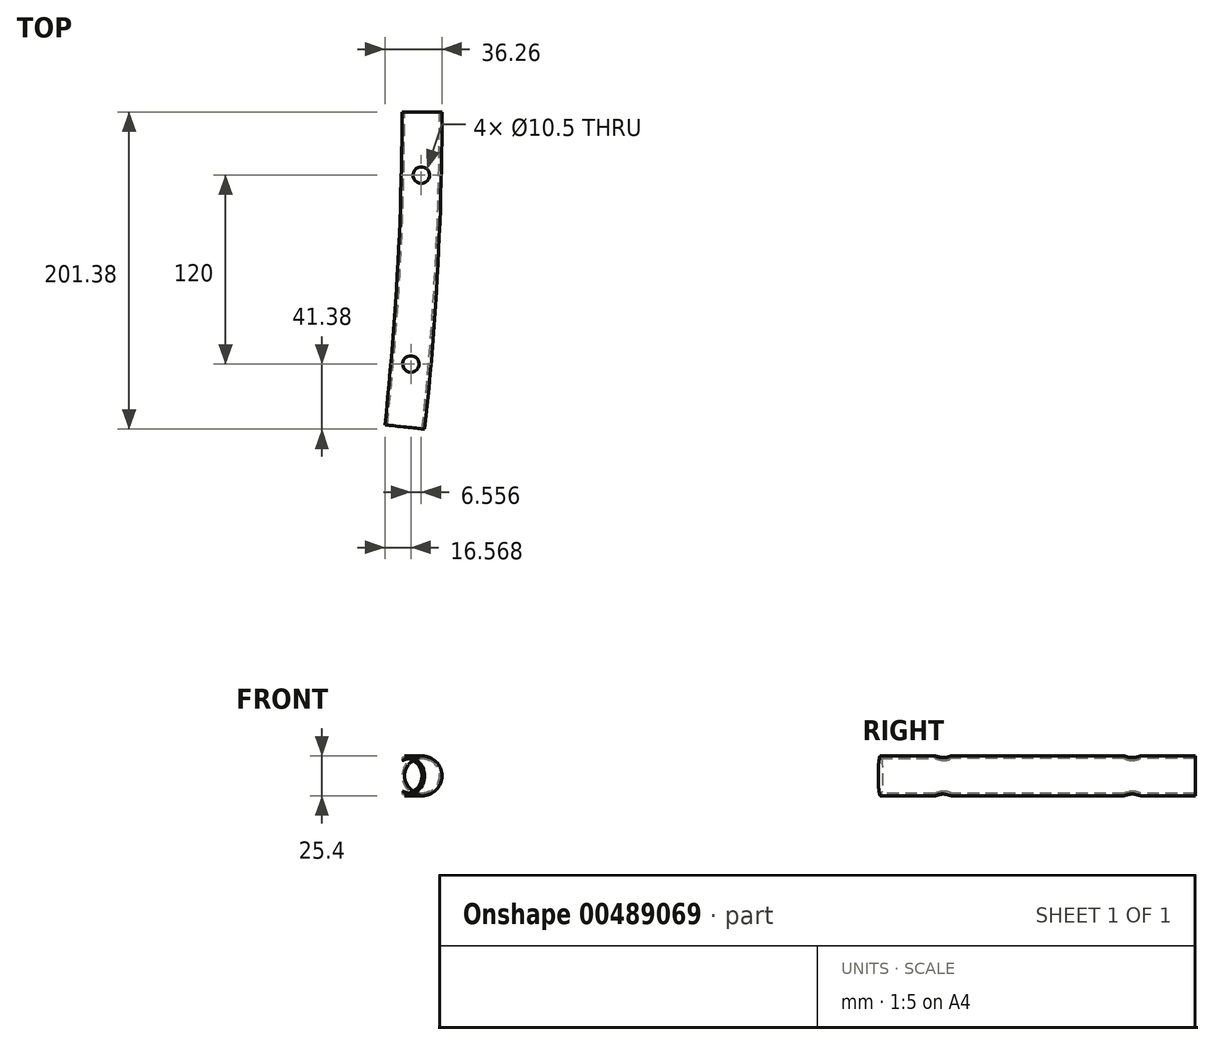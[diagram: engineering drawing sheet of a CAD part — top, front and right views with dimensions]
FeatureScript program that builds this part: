
annotation { "Feature Type Name" : "Feature", "Feature Type Description" : "" }
export const myFeature = defineFeature(function(context is Context, id is Id, definition is map)
    precondition{}
    {
        {
            var Q0;
            Q0=qCreatedBy(makeId("Top.planeOp"),FACE);
            var sketch = newSketch(context, id + "F0", { "sketchPlane" : qUnion([Q0])});
            skArc(sketch, "E0", {"start": v(1823.16, -200) * mm, "mid": v(1831.36, -100.15) * mm, "end": v(1834.1, 0) * mm});
            skSolve(sketch);
        }
        {
            var Q0;
            Q0=qCreatedBy(makeId("Front.planeOp"),FACE);
            var sketch = newSketch(context, id + "F1", { "sketchPlane" : qUnion([Q0])});
            skCircle(sketch, "E1", {"center": v(1834.1, 0) * mm, "radius": 12.7 * mm});
            skCircle(sketch, "E2.0", {"center": v(1834.1, 0) * mm, "radius": 11.1 * mm});
            skSolve(sketch);
        }
        {
            var Q0;
            Q0 = qSketchRegion(id + "F1", true);
            var Q1;
            Q1 = qConstructionFilter(qBodyType(qCreatedBy(id + "F0" ,EDGE), BodyType.WIRE), ConstructionObject.NO);
            sweep(context, id + "F2", {"profiles" : qUnion([Q0]), "path" : qUnion([Q1])});
        }
        {
            var Q0;
            Q0=qCreatedBy(makeId("Top.planeOp"),FACE);
            var sketch = newSketch(context, id + "F3", { "sketchPlane" : qUnion([Q0])});
            skArc(sketch, "E3", {"start": v(1834.1, 0) * mm, "mid": v(1831.36, -100.15) * mm, "end": v(1823.16, -200) * mm, "construction": true});
            skCircle(sketch, "E4", {"center": v(1833.66, -40) * mm, "radius": 5.25 * mm});
            skCircle(sketch, "E5", {"center": v(1827.1, -160) * mm, "radius": 5.25 * mm});
            skSolve(sketch);
        }
        {
            var Q0;
            Q0 = qSketchRegion(id + "F3", true);
            extrude(context, id + "F4", {"entities" : qUnion([Q0]), "operationType" : NewBodyOperationType.REMOVE, "endBound" : BoundingType.THROUGH_ALL, "oppositeDirection" : true, "depth" : 25 * mm, "hasSecondDirection" : true, "secondDirectionBound" : BoundingType.THROUGH_ALL, "secondDirectionOppositeDirection" : false, "secondDirectionDepth" : 25 * mm});
        }
    });
